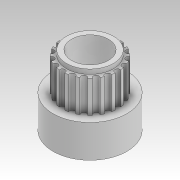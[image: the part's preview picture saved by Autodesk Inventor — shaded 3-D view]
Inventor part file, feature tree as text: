
AUTODESK INVENTOR PART (.ipt)
format: ipt  version: 2020 (Build 240168000, 168)  size: 195,584 bytes
history: native  units: mm
features: sketch x3, extrude x2, pattern_circular x2, revolve x1
ambient origin geometry x8: Origin, YZ Plane, XZ Plane, XY Plane, X Axis, Y Axis, Z Axis, Center Point
bodies: Solid1 (feature_tree)
feature tree (8):
  revolve  "Revolution1"  [1 undecoded]
  extrude  "Extrusion1"  Depth=6.11mm
  pattern_circular  "Circular Pattern1"  [2 undecoded]
  extrude  "Extrusion2"  TaperAngle=90.0deg  [1 undecoded]
  pattern_circular  "Circular Pattern2"  [2 undecoded]
  sketch  "Sketch1"  dims[d0=7.0mm d1=7.1mm]
  sketch  "Sketch2"  dims[d2=8.0mm d3=6.11mm]
  sketch  "Sketch3"  dims[d5=1.0mm d6=1.0mm d7=90.0deg d8=1.2mm d9=6.0mm d10=10.0mm d11=0.0mm d12=200.0mm d13=360.0deg d15=4.0mm d16=2.5mm d17=10.0mm d18=0.0mm d19=20.0mm d20=90.0deg]
note: 6 required parameter values undecoded (feature->parameter linkage not recoverable at this tier; creation-order binding heuristic only, values carry confidence <= 0.55)